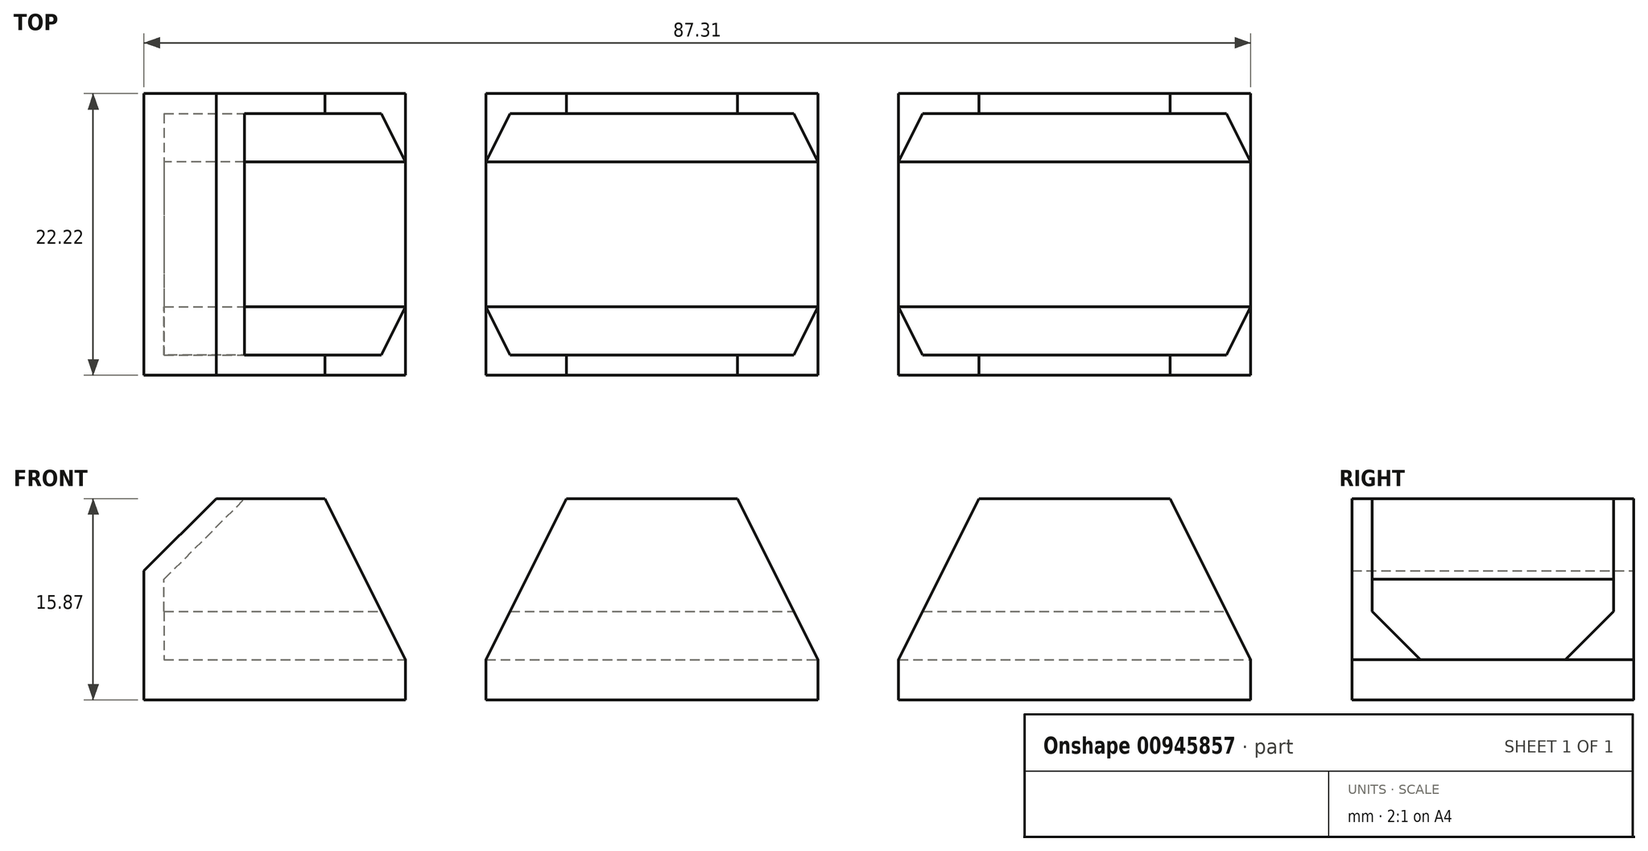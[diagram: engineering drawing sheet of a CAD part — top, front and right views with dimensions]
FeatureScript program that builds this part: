
annotation { "Feature Type Name" : "Feature", "Feature Type Description" : "" }
export const myFeature = defineFeature(function(context is Context, id is Id, definition is map)
    precondition{}
    {
        {
            var Q0;
            Q0=qCreatedBy(makeId("Front.planeOp"),FACE);
            var sketch = newSketch(context, id + "F0", { "sketchPlane" : qUnion([Q0])});
            skLineSegment(sketch, "E0.bottom", {"start": v(4.76, 0) * mm, "end": v(-21.43, 0) * mm});
            skLineSegment(sketch, "E0.top", {"start": v(4.76, -3.18) * mm, "end": v(-21.43, -3.18) * mm});
            skLineSegment(sketch, "E0.left", {"start": v(4.76, 0) * mm, "end": v(4.76, -3.17) * mm});
            skLineSegment(sketch, "E0.right", {"start": v(-21.43, 0) * mm, "end": v(-21.43, -3.18) * mm});
            skLineSegment(sketch, "E1", {"start": v(-21.43, 0) * mm, "end": v(-15.08, 0) * mm});
            skLineSegment(sketch, "E2", {"start": v(-15.08, 0) * mm, "end": v(-15.08, 12.7) * mm});
            skLineSegment(sketch, "E3", {"start": v(4.76, 0) * mm, "end": v(-1.59, 0) * mm});
            skLineSegment(sketch, "E4", {"start": v(-1.59, 0) * mm, "end": v(-1.59, 12.7) * mm});
            skLineSegment(sketch, "E5", {"start": v(-1.59, 12.7) * mm, "end": v(-15.08, 12.7) * mm});
            skLineSegment(sketch, "E6", {"start": v(-15.08, 12.7) * mm, "end": v(-21.43, 0) * mm});
            skLineSegment(sketch, "E7", {"start": v(-1.59, 12.7) * mm, "end": v(4.76, 0) * mm});
            skLineSegment(sketch, "E8", {"start": v(-21.43, 0) * mm, "end": v(-27.78, 0) * mm});
            skLineSegment(sketch, "E9", {"start": v(-27.78, 0) * mm, "end": v(-27.78, -3.18) * mm});
            skLineSegment(sketch, "E10", {"start": v(4.76, -3.17) * mm, "end": v(11.11, -3.17) * mm});
            skLineSegment(sketch, "E11", {"start": v(11.11, -3.17) * mm, "end": v(38.9, -3.17) * mm});
            skLineSegment(sketch, "E12", {"start": v(38.9, -3.17) * mm, "end": v(38.9, 0) * mm});
            skLineSegment(sketch, "E13", {"start": v(38.9, 0) * mm, "end": v(11.11, 0) * mm});
            skLineSegment(sketch, "E14", {"start": v(11.11, 0) * mm, "end": v(11.11, -3.17) * mm});
            skLineSegment(sketch, "E15", {"start": v(-27.78, 0) * mm, "end": v(-46.83, 0) * mm});
            skLineSegment(sketch, "E16", {"start": v(-46.83, 0) * mm, "end": v(-46.83, -3.17) * mm});
            skLineSegment(sketch, "E17", {"start": v(-46.83, -3.18) * mm, "end": v(-27.78, -3.18) * mm});
            skLineSegment(sketch, "E18", {"start": v(-27.78, 0) * mm, "end": v(-34.13, 0) * mm});
            skLineSegment(sketch, "E19", {"start": v(-34.13, 0) * mm, "end": v(-34.13, 12.7) * mm});
            skLineSegment(sketch, "E20", {"start": v(-46.83, 0) * mm, "end": v(-40.48, 0) * mm});
            skLineSegment(sketch, "E21", {"start": v(-40.48, 0) * mm, "end": v(-40.48, 12.7) * mm});
            skLineSegment(sketch, "E22", {"start": v(-40.48, 12.7) * mm, "end": v(-34.13, 12.7) * mm});
            skLineSegment(sketch, "E23", {"start": v(-34.13, 12.7) * mm, "end": v(-27.78, 0) * mm});
            skLineSegment(sketch, "E24", {"start": v(-46.83, 0) * mm, "end": v(-46.83, 6.35) * mm});
            skLineSegment(sketch, "E25", {"start": v(-46.83, 6.35) * mm, "end": v(-40.48, 12.7) * mm});
            skLineSegment(sketch, "E26", {"start": v(11.11, 0) * mm, "end": v(17.46, 0) * mm});
            skLineSegment(sketch, "E27", {"start": v(17.46, 0) * mm, "end": v(17.46, 12.7) * mm});
            skLineSegment(sketch, "E28", {"start": v(38.9, 0) * mm, "end": v(32.54, 0) * mm});
            skLineSegment(sketch, "E29", {"start": v(32.54, 0) * mm, "end": v(32.54, 12.7) * mm});
            skLineSegment(sketch, "E30", {"start": v(32.54, 12.7) * mm, "end": v(17.46, 12.7) * mm});
            skLineSegment(sketch, "E31", {"start": v(17.46, 12.7) * mm, "end": v(11.11, 0) * mm});
            skLineSegment(sketch, "E32", {"start": v(32.54, 12.7) * mm, "end": v(38.9, 0) * mm});
            skLineSegment(sketch, "E33", {"start": v(-46.83, -3.17) * mm, "end": v(-48.42, -3.17) * mm});
            skLineSegment(sketch, "E34", {"start": v(-48.42, -3.17) * mm, "end": v(-48.42, 6.35) * mm});
            skLineSegment(sketch, "E35", {"start": v(-48.42, 7) * mm, "end": v(-48.42, 6.35) * mm});
            skLineSegment(sketch, "E36", {"start": v(-40.48, 12.7) * mm, "end": v(-42.73, 12.7) * mm});
            skLineSegment(sketch, "E37", {"start": v(-48.42, 7) * mm, "end": v(-42.73, 12.7) * mm});
            skSolve(sketch);
        }
        {
            var Q0;
            {var subQ0=sQuery(id+"F0.wireOp",EDGE,"E21");Q0=makeQuery(id+"F0.imprint","IMPRINT",FACE,{"disambiguationData":[TD([[makeQuery(id+"F0.imprint","IMPRINT",EDGE,{"derivedFrom":subQ0}),1.0]])]});}
            var Q1;
            {var subQ2=sQuery(id+"F0.wireOp",EDGE,"E2");Q1=makeQuery(id+"F0.imprint","IMPRINT",FACE,{"disambiguationData":[TD([[makeQuery(id+"F0.imprint","IMPRINT",EDGE,{"derivedFrom":subQ2}),1.0]])]});}
            var Q2;
            {var subQ0=sQuery(id+"F0.wireOp",EDGE,"E4");Q2=makeQuery(id+"F0.imprint","IMPRINT",FACE,{"disambiguationData":[TD([[makeQuery(id+"F0.imprint","IMPRINT",EDGE,{"derivedFrom":subQ0}),-1.0]])]});}
            var Q3;
            {var subQ2=sQuery(id+"F0.wireOp",EDGE,"E19");Q3=makeQuery(id+"F0.imprint","IMPRINT",FACE,{"disambiguationData":[TD([[makeQuery(id+"F0.imprint","IMPRINT",EDGE,{"derivedFrom":subQ2}),-1.0]])]});}
            var Q4;
            {var subQ2=sQuery(id+"F0.wireOp",EDGE,"E27");Q4=makeQuery(id+"F0.imprint","IMPRINT",FACE,{"disambiguationData":[TD([[makeQuery(id+"F0.imprint","IMPRINT",EDGE,{"derivedFrom":subQ2}),1.0]])]});}
            var Q5;
            {var subQ2=sQuery(id+"F0.wireOp",EDGE,"E29");Q5=makeQuery(id+"F0.imprint","IMPRINT",FACE,{"disambiguationData":[TD([[makeQuery(id+"F0.imprint","IMPRINT",EDGE,{"derivedFrom":subQ2}),-1.0]])]});}
            var Q6;
            Q6=makeQuery(id+"F0.imprint","IMPRINT",FACE,{"disambiguationData":[TD([[makeQuery(id+"F0.imprint","IMPRINT",EDGE,{"derivedFrom":sQuery(id+"F0.wireOp",EDGE,"E0.top")}),-1.0]])]});
            var Q7;
            {var subQ2=sQuery(id+"F0.wireOp",EDGE,"E2");Q7=makeQuery(id+"F0.imprint","IMPRINT",FACE,{"disambiguationData":[TD([[makeQuery(id+"F0.imprint","IMPRINT",EDGE,{"derivedFrom":subQ2}),-1.0]])]});}
            var Q8;
            Q8=makeQuery(id+"F0.imprint","IMPRINT",FACE,{"disambiguationData":[TD([[makeQuery(id+"F0.imprint","IMPRINT",EDGE,{"derivedFrom":sQuery(id+"F0.wireOp",EDGE,"E11")}),1.0]])]});
            var Q9;
            {var subQ2=sQuery(id+"F0.wireOp",EDGE,"E27");Q9=makeQuery(id+"F0.imprint","IMPRINT",FACE,{"disambiguationData":[TD([[makeQuery(id+"F0.imprint","IMPRINT",EDGE,{"derivedFrom":subQ2}),-1.0]])]});}
            var Q10;
            Q10=makeQuery(id+"F0.imprint","IMPRINT",FACE,{"disambiguationData":[TD([[makeQuery(id+"F0.imprint","IMPRINT",EDGE,{"derivedFrom":sQuery(id+"F0.wireOp",EDGE,"E16")}),-1.0]])]});
            var Q11;
            Q11=makeQuery(id+"F0.imprint","IMPRINT",FACE,{"disambiguationData":[TD([[makeQuery(id+"F0.imprint","IMPRINT",EDGE,{"derivedFrom":sQuery(id+"F0.wireOp",EDGE,"E22")}),1.0]])]});
            var Q12;
            {var subQ3=sQuery(id+"F0.wireOp",EDGE,"E9");Q12=makeQuery(id+"F0.imprint","IMPRINT",FACE,{"disambiguationData":[TD([[makeQuery(id+"F0.imprint","IMPRINT",EDGE,{"derivedFrom":subQ3}),-1.0]])]});}
            var Q13;
            {var subQ2=sQuery(id+"F0.wireOp",EDGE,"E19");Q13=makeQuery(id+"F0.imprint","IMPRINT",FACE,{"disambiguationData":[TD([[makeQuery(id+"F0.imprint","IMPRINT",EDGE,{"derivedFrom":subQ2}),1.0]])]});}
            extrude(context, id + "F1", {"entities" : qUnion([Q0, Q1, Q2, Q3, Q4, Q5, Q6, Q7, Q8, Q9, Q10, Q11, Q12, Q13]), "endBound" : BoundingType.SYMMETRIC, "depth" : 22.22 * mm, "offsetDistance" : 25.4 * mm});
        }
        {
            var Q0;
            {var subQ0=sQuery(id+"F0.wireOp",EDGE,"E21");Q0=makeQuery(id+"F0.imprint","IMPRINT",FACE,{"disambiguationData":[TD([[makeQuery(id+"F0.imprint","IMPRINT",EDGE,{"derivedFrom":subQ0}),1.0]])]});}
            var Q1;
            {var subQ2=sQuery(id+"F0.wireOp",EDGE,"E19");Q1=makeQuery(id+"F0.imprint","IMPRINT",FACE,{"disambiguationData":[TD([[makeQuery(id+"F0.imprint","IMPRINT",EDGE,{"derivedFrom":subQ2}),1.0]])]});}
            var Q2;
            {var subQ2=sQuery(id+"F0.wireOp",EDGE,"E19");Q2=makeQuery(id+"F0.imprint","IMPRINT",FACE,{"disambiguationData":[TD([[makeQuery(id+"F0.imprint","IMPRINT",EDGE,{"derivedFrom":subQ2}),-1.0]])]});}
            var Q3;
            {var subQ2=sQuery(id+"F0.wireOp",EDGE,"E2");Q3=makeQuery(id+"F0.imprint","IMPRINT",FACE,{"disambiguationData":[TD([[makeQuery(id+"F0.imprint","IMPRINT",EDGE,{"derivedFrom":subQ2}),-1.0]])]});}
            var Q4;
            {var subQ2=sQuery(id+"F0.wireOp",EDGE,"E2");Q4=makeQuery(id+"F0.imprint","IMPRINT",FACE,{"disambiguationData":[TD([[makeQuery(id+"F0.imprint","IMPRINT",EDGE,{"derivedFrom":subQ2}),1.0]])]});}
            var Q5;
            {var subQ0=sQuery(id+"F0.wireOp",EDGE,"E4");Q5=makeQuery(id+"F0.imprint","IMPRINT",FACE,{"disambiguationData":[TD([[makeQuery(id+"F0.imprint","IMPRINT",EDGE,{"derivedFrom":subQ0}),-1.0]])]});}
            var Q6;
            {var subQ2=sQuery(id+"F0.wireOp",EDGE,"E27");Q6=makeQuery(id+"F0.imprint","IMPRINT",FACE,{"disambiguationData":[TD([[makeQuery(id+"F0.imprint","IMPRINT",EDGE,{"derivedFrom":subQ2}),1.0]])]});}
            var Q7;
            {var subQ2=sQuery(id+"F0.wireOp",EDGE,"E27");Q7=makeQuery(id+"F0.imprint","IMPRINT",FACE,{"disambiguationData":[TD([[makeQuery(id+"F0.imprint","IMPRINT",EDGE,{"derivedFrom":subQ2}),-1.0]])]});}
            var Q8;
            {var subQ2=sQuery(id+"F0.wireOp",EDGE,"E29");Q8=makeQuery(id+"F0.imprint","IMPRINT",FACE,{"disambiguationData":[TD([[makeQuery(id+"F0.imprint","IMPRINT",EDGE,{"derivedFrom":subQ2}),-1.0]])]});}
            extrude(context, id + "F2", {"entities" : qUnion([Q0, Q1, Q2, Q3, Q4, Q5, Q6, Q7, Q8]), "operationType" : NewBodyOperationType.REMOVE, "endBound" : BoundingType.SYMMETRIC, "oppositeDirection" : true, "depth" : 19.05 * mm, "offsetDistance" : 25.4 * mm});
        }
        {
            var Q0;
            Q0=makeQuery(id+"F2.boolean.opBoolean","COPY",EDGE,{"derivedFrom":makeQuery(id+"F2.opExtrude","CAP_EDGE",EDGE,{"disambiguationData":[OSD([sQuery(id+"F0.wireOp",EDGE,"E15")])],"isStart":true})});
            var Q1;
            Q1=makeQuery(id+"F2.boolean.opBoolean","COPY",EDGE,{"derivedFrom":makeQuery(id+"F2.opExtrude","CAP_EDGE",EDGE,{"disambiguationData":[OSD([sQuery(id+"F0.wireOp",EDGE,"E15")])],"isStart":false})});
            var Q2;
            Q2=makeQuery(id+"F2.boolean.opBoolean","COPY",EDGE,{"derivedFrom":makeQuery(id+"F2.opExtrude","CAP_EDGE",EDGE,{"disambiguationData":[OSD([sQuery(id+"F0.wireOp",EDGE,"E0.bottom")])],"isStart":false})});
            var Q3;
            Q3=makeQuery(id+"F2.boolean.opBoolean","COPY",EDGE,{"derivedFrom":makeQuery(id+"F2.opExtrude","CAP_EDGE",EDGE,{"disambiguationData":[OSD([sQuery(id+"F0.wireOp",EDGE,"E13")])],"isStart":false})});
            var Q4;
            Q4=makeQuery(id+"F2.boolean.opBoolean","COPY",EDGE,{"derivedFrom":makeQuery(id+"F2.opExtrude","CAP_EDGE",EDGE,{"disambiguationData":[OSD([sQuery(id+"F0.wireOp",EDGE,"E0.bottom")])],"isStart":true})});
            var Q5;
            Q5=makeQuery(id+"F2.boolean.opBoolean","COPY",EDGE,{"derivedFrom":makeQuery(id+"F2.opExtrude","CAP_EDGE",EDGE,{"disambiguationData":[OSD([sQuery(id+"F0.wireOp",EDGE,"E13")])],"isStart":true})});
            chamfer(context, id + "F3", {"entities" : qUnion([Q0, Q1, Q2, Q3, Q4, Q5]), "width" : 3.8 * mm, "tangentPropagation" : true});
        }
    });
